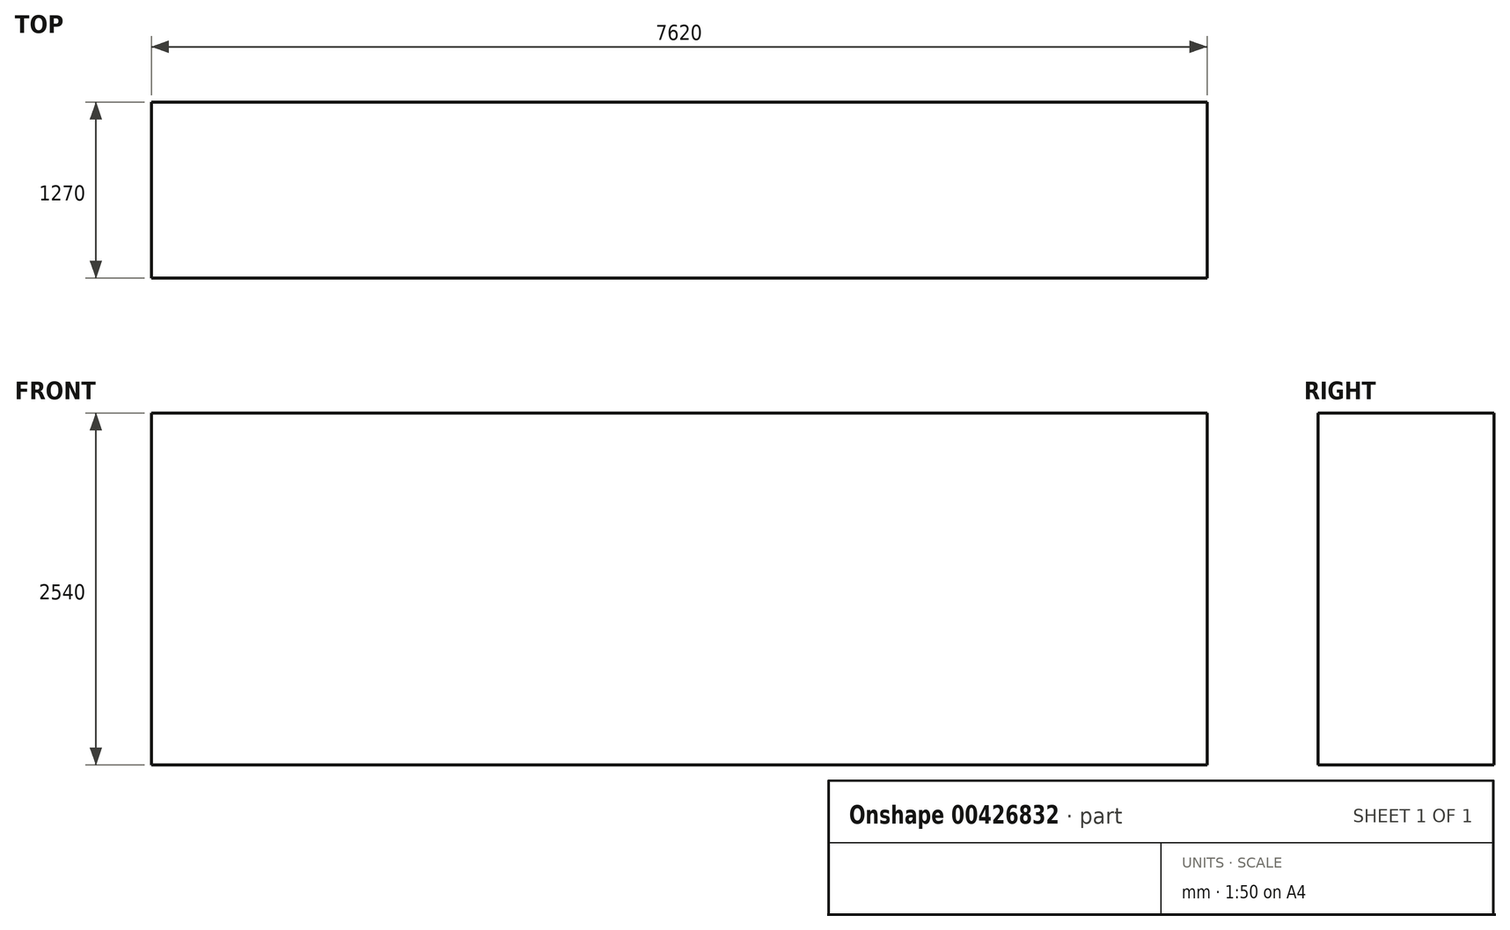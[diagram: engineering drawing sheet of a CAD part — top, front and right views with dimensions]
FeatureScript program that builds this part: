
annotation { "Feature Type Name" : "Feature", "Feature Type Description" : "" }
export const myFeature = defineFeature(function(context is Context, id is Id, definition is map)
    precondition{}
    {
        {
            var Q0;
            Q0=qCreatedBy(makeId("Front.planeOp"),FACE);
            var sketch = newSketch(context, id + "F0", { "sketchPlane" : qUnion([Q0])});
            skLineSegment(sketch, "E0.bottom", {"start": v(-3810, 1270) * mm, "end": v(3810, 1270) * mm});
            skLineSegment(sketch, "E0.top", {"start": v(-3810, -1270) * mm, "end": v(3810, -1270) * mm});
            skLineSegment(sketch, "E0.left", {"start": v(-3810, 1270) * mm, "end": v(-3810, -1270) * mm});
            skLineSegment(sketch, "E0.right", {"start": v(3810, 1270) * mm, "end": v(3810, -1270) * mm});
            skPoint(sketch, "E0.middle", {"position": v(0, 0) * mm});
            skSolve(sketch);
        }
        {
            var Q0;
            Q0=makeQuery(id+"F0.imprint","IMPRINT",FACE,{"disambiguationData":[TD([[makeQuery(id+"F0.imprint","IMPRINT",EDGE,{"derivedFrom":sQuery(id+"F0.wireOp",EDGE,"E0.bottom")}),-1.0]])]});
            extrude(context, id + "F1", {"entities" : qUnion([Q0]), "depth" : 1270 * mm});
        }
    });
